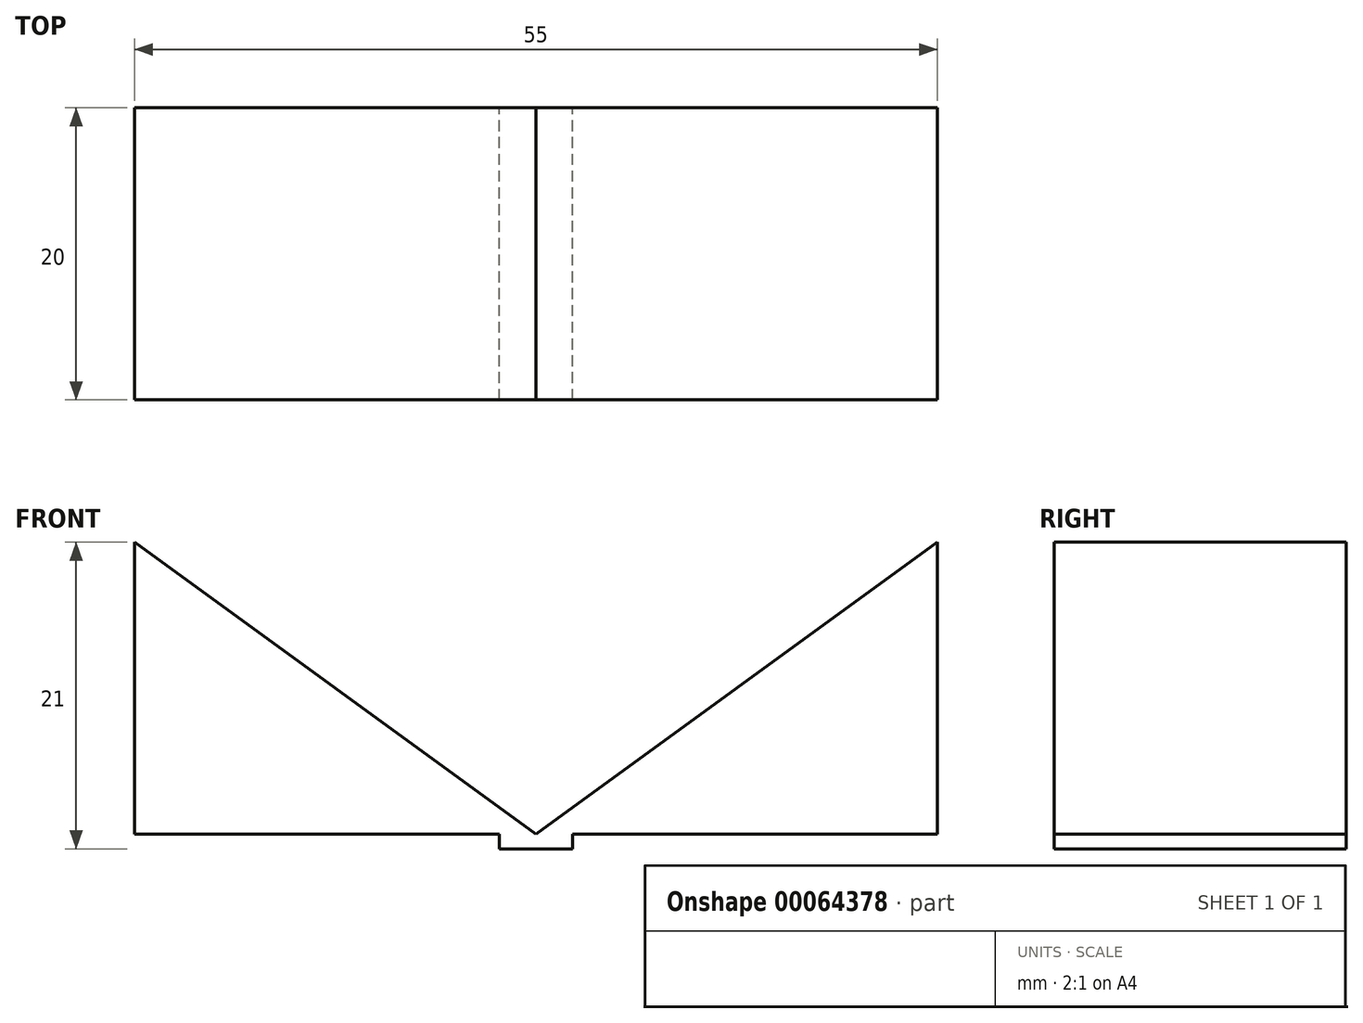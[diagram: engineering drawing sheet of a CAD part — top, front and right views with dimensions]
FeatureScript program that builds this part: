
annotation { "Feature Type Name" : "Feature", "Feature Type Description" : "" }
export const myFeature = defineFeature(function(context is Context, id is Id, definition is map)
    precondition{}
    {
        {
            var Q0;
            Q0=qCreatedBy(makeId("Front.planeOp"),FACE);
            var sketch = newSketch(context, id + "F0", { "sketchPlane" : qUnion([Q0])});
            skLineSegment(sketch, "E0.rect.top", {"start": v(2.5, -0.5) * mm, "end": v(-2.5, -0.5) * mm});
            skLineSegment(sketch, "E0.rect.left", {"start": v(2.5, 0.5) * mm, "end": v(2.5, -0.5) * mm});
            skLineSegment(sketch, "E0.rect.right", {"start": v(-2.5, 0.5) * mm, "end": v(-2.5, -0.5) * mm});
            skPoint(sketch, "E0.rect.middle", {"position": v(0, 0) * mm});
            skLineSegment(sketch, "E1", {"start": v(2.5, 0.5) * mm, "end": v(27.5, 0.5) * mm});
            skLineSegment(sketch, "E2", {"start": v(27.5, 0.5) * mm, "end": v(27.5, 20.5) * mm});
            skLineSegment(sketch, "E3", {"start": v(27.5, 20.5) * mm, "end": v(0, 0.5) * mm});
            skLineSegment(sketch, "E4", {"start": v(0, 0.5) * mm, "end": v(-27.5, 20.5) * mm});
            skLineSegment(sketch, "E5", {"start": v(-27.5, 20.5) * mm, "end": v(-27.5, 0.5) * mm});
            skLineSegment(sketch, "E6", {"start": v(-27.5, 0.5) * mm, "end": v(-2.5, 0.5) * mm});
            skSolve(sketch);
        }
        {
            var Q0;
            Q0 = qSketchRegion(id + "F0", true);
            extrude(context, id + "F1", {"entities" : qUnion([Q0]), "depth" : 20 * mm});
        }
    });
